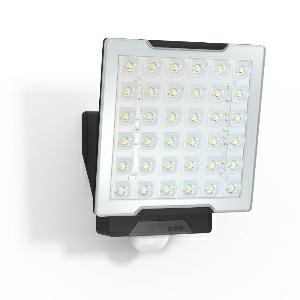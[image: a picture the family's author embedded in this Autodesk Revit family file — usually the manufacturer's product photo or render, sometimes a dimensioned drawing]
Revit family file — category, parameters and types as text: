
# Revit family: xled_pro_square_010027
name_source: partatom
category: Leuchten
revit_build: Autodesk Revit 2016 (Build: 20190508_0715(x64)
units: mm (PartAtom-declared; Revit-internal decimal feet)

## family parameters
Basisbauteil = Fläche
Beim Laden mit Abzugskörper schneiden = Nein
Bemaßung runder Anschluss = Durchmesser verwenden
Gemeinsam genutzt = Nein
Lichtquelle = Nein
Raumberechnungspunkt = Nein
Teiletyp = Normal

## types (1)
- XLED PRO Square (1 x , 2400 lm, 4000 K)
    Beschreibung = Dimensions (L x W x H): 130 x 178 x 230 mm; Mains power supply: 220 – 240 V / 50 – 60 Hz; Mounting height max.: 6,00 m; Sensor Technology: passive infrared; Output: 24,8 W; Interconnection: Yes; Luminous flux: 2400 lm; Colour temperature: 4000 K; Colour variation LED: SDCM3; Colour Rendering Index CRI: 80-89; With lamp: Yes, STEINEL LED system; Lamp: LED cannot be replaced; LED life expectancy (max. °C): 50000 h; LED cooling system: Passive Thermo Control; With motion detector: Yes; Detection angle: 240 °; Angle of aperture: 180 °; Sneak-by guard: Yes; Capability of masking out individual segments: Yes; Reach, radial: r = 3 m (19 m²); Reach, tangential: r = 12 m (302 m²); Photo-cell controller: Yes; Twilight setting: 2 – 1000 lx; Time setting: 5 sec – 15 min; Basic light level function: Yes; Basic light level function time: 10/30 min, all night; Functions: Sensor channel, Actuator channel; Soft light start: No; Continuous light: selectable; Impact resistance: IK03; IP-rating: IP54; Protection class: I; Ambient temperature: -20 – 40 °C; Housing material: Aluminium; Cover material: Plastic, transparent; Manufacturer's Warranty: 5 years; PU1, net weight: 1,6 kg; Version: eNet - black; PU1, EAN: 4007841010027
    CIE Flux Codes = 52 86 98 99 100
    Color Rendering = 80-89
    Color Temperature = 4000 K
    Frequency = 60 Hz, 50 Hz
    Height = 230 mm
    Hersteller = Steinel
    Lamp Light Flux = 2400 lm
    Lamp count = 1
    Lampe = 1 x
    Length = 130 mm
    Luminous efficacy = 100 lm/W
    ModVariant = Nein
    Modell = 010027
    Mounting Type = Surface mounted
    Number of Poles = 1
    OnlyDefault = Ja
    Power Factor = 1
    Product Name = XLED PRO Square
    Product group = Sensor-switched indoor light
    ProductGroupID = 30
    Protection Class = Protection class I
    Protection Degree = IP 54
    RlxData = <blob elided: 133785 chars, md5=53386f9e>
    Scheinlast = 24 VA
    Socket = socket
    Standby Power = 0 W
    System Light Flux = 2400 lm
    System Power = 24 W
    Typenbild = produkt1_010027.jpg
    Typenkommentare = Product without accessories
    URL = http://relux.com
    VarID = ---
    Voltage = 0 V
    Vorgabe-Ansicht = 1800 mm
    Weight = 0.00 kg
    Width = 178 mm

## geometry (parser evidence)
native form markers: Sweep x14
no freeform markers — native parametric forms only
